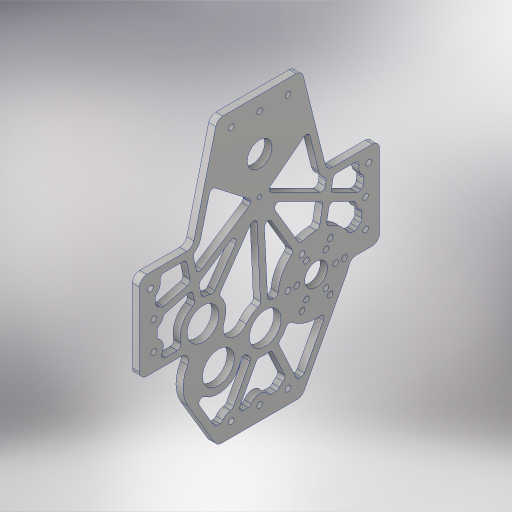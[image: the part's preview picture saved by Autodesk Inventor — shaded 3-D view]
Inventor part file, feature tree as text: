
AUTODESK INVENTOR PART (.ipt)
format: ipt  version: 2023.4 (Build 274418000, 418)  size: 897,536 bytes
history: native  units: in
note: dims shown in document units (in); Inventor stores cm internally (conversion verified against a paired STEP export)
features: sketch x4, hole x3, extrude x2, fillet x2, projected_geometry x2
ambient origin geometry x8: Origin, YZ Plane, XZ Plane, XY Plane, X Axis, Y Axis, Z Axis, Center Point
bodies: Solid1 (feature_tree)
feature tree (13):
  sketch  "Sketch1"  dims[d0=10.0in d1=1.0in]
  sketch  "Sketch2"  dims[d2=3.25in d3=1.0in]
  extrude  "Extrusion1"  Depth=10.0in
  hole  "Mount Holes"  [1 undecoded]
  hole  "Motor Mount Holes"  [1 undecoded]
  fillet  "Fillet1"  Radius=0.123in
  hole  "Hole4"  [1 undecoded]
  extrude  "Extrusion4"  Depth=0.13in
  fillet  "Fillet3"  Radius=3.3in
  sketch  "Sketch8"  dims[d4=1.942in d6=3.5in d7=0.123in]
  sketch  "Sketch9"  dims[d8=1.0in d9=1.0in d10=0.6in d11=3.3in d12=0.9in d13=2.5in d14=1.2in d15=2.2in d16=2.4in d19=2.5in d23=0.8in d24=1.125in d26=1.0in d27=1.0in d28=1.0in d29=1.0in d30=0.25in d31=0.25in d32=0.25in d33=1.375in d34=2.0in d35=2.3622in d37=360.0deg d41=0.125in d42=3.0in d44=0.25in d45=0.0in d46=0.201in d47=0.75in d48=0.385in d49=0.25in d50=0.5635in d51=1.0in d52=0.8108in d53=0.201in d54=0.75in d55=0.375in d56=0.25in d57=0.5635in d58=1.0in d59=0.8108in d60=4.006in d63=1.25in d64=1.75in d66=1.375in d67=1.25in d68=0.875in d70=0.375in d71=1.875in d73=4.6532in d74=0.5in d75=1.432in d76=4.297in d77=0.26in d78=0.391in d79=0.391in d123=4.651in d133=8.0944in d134=1.8013in d135=4.4272in d141=0.875in d162=2.624in d163=0.156in d164=0.38in d165=0.385in d166=0.25in d167=0.5635in d168=1.0in d169=0.8108in d170=0.25in d171=0.25in d172=0.25in d173=0.25in d174=0.25in d175=0.25in d176=0.25in d177=0.25in d178=0.25in d179=0.25in d180=0.25in d181=0.25in d182=0.25in d183=0.25in d184=0.25in d185=0.25in d186=0.125in d187=0.125in d188=0.125in d189=0.125in d190=0.125in d191=0.125in d192=0.125in d193=0.125in d194=0.125in d195=0.125in d196=0.125in d197=0.125in d198=0.125in d199=0.125in d200=0.125in d201=0.125in d202=0.125in d203=0.125in d204=0.125in d205=0.125in d207=0.0in d208=0.0in d209=0.13in d210=0.125in d211=0.125in]
  projected_geometry  "Project Cut Edges5"
  projected_geometry  "Project Cut Edges6"
note: 3 required parameter values undecoded (feature->parameter linkage not recoverable at this tier; creation-order binding heuristic only, values carry confidence <= 0.55)
